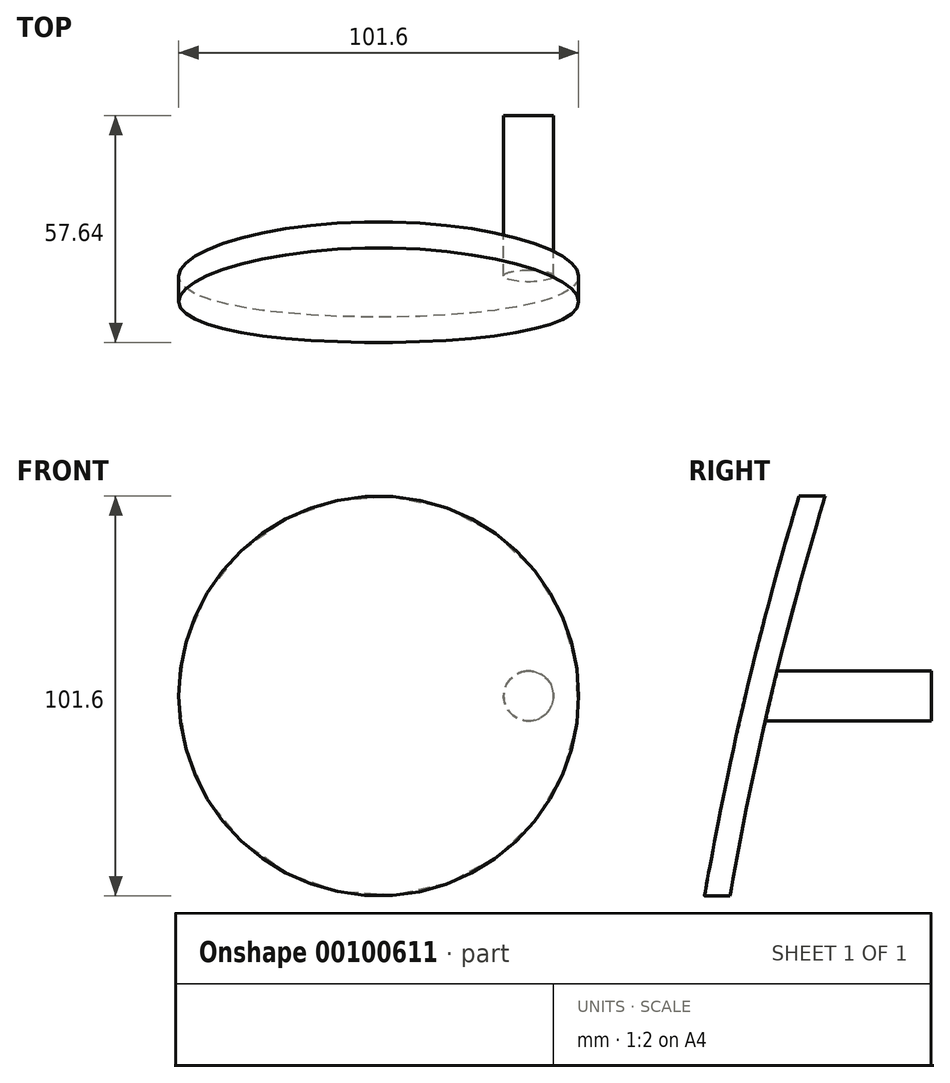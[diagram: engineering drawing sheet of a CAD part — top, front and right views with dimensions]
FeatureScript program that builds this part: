
annotation { "Feature Type Name" : "Feature", "Feature Type Description" : "" }
export const myFeature = defineFeature(function(context is Context, id is Id, definition is map)
    precondition{}
    {
        {
            var Q0;
            Q0=qCreatedBy(makeId("Right.planeOp"),FACE);
            var sketch = newSketch(context, id + "F0", { "sketchPlane" : qUnion([Q0])});
            skArc(sketch, "E0", {"start": v(-794.07, 323.85) * mm, "mid": v(-857.57, 0) * mm, "end": v(-794.07, -323.85) * mm});
            skLineSegment(sketch, "E1", {"start": v(-794.07, 323.85) * mm, "end": v(-794.07, -323.85) * mm});
            skSolve(sketch);
        }
        {
            var Q0;
            Q0 = qSketchRegion(id + "F0", true);
            extrude(context, id + "F1", {"entities" : qUnion([Q0]), "endBound" : BoundingType.SYMMETRIC, "depth" : 101.6 * mm});
        }
        {
            var Q0;
            Q0=qCreatedBy(makeId("Right.planeOp"),FACE);
            var sketch = newSketch(context, id + "F2", { "sketchPlane" : qUnion([Q0])});
            skCircle(sketch, "E2", {"center": v(0, 0) * mm, "radius": 851.22 * mm});
            skSolve(sketch);
        }
        {
            var Q0;
            Q0 = qSketchRegion(id + "F2", true);
            extrude(context, id + "F3", {"entities" : qUnion([Q0]), "operationType" : NewBodyOperationType.REMOVE, "endBound" : BoundingType.SYMMETRIC, "oppositeDirection" : true, "depth" : 101.6 * mm});
        }
        {
            var Q0;
            Q0=qCreatedBy(makeId("Front.planeOp"),FACE);
            var sketch = newSketch(context, id + "F4", { "sketchPlane" : qUnion([Q0])});
            skCircle(sketch, "E3", {"center": v(0, 196.85) * mm, "radius": 50.8 * mm});
            skLineSegment(sketch, "E4.bottom", {"start": v(-127, 381) * mm, "end": v(127, 381) * mm});
            skLineSegment(sketch, "E4.top", {"start": v(-127, -381) * mm, "end": v(127, -381) * mm});
            skLineSegment(sketch, "E4.left", {"start": v(-127, 381) * mm, "end": v(-127, -381) * mm});
            skLineSegment(sketch, "E4.right", {"start": v(127, 381) * mm, "end": v(127, -381) * mm});
            skSolve(sketch);
        }
        {
            var Q0;
            Q0=makeQuery(id+"F4.imprint","IMPRINT",FACE,{"disambiguationData":[TD([[makeQuery(id+"F4.imprint","IMPRINT",EDGE,{"derivedFrom":sQuery(id+"F4.wireOp",EDGE,"E3")}),-1.0]])]});
            extrude(context, id + "F5", {"entities" : qUnion([Q0]), "operationType" : NewBodyOperationType.REMOVE, "endBound" : BoundingType.THROUGH_ALL, "depth" : 25.4 * mm});
        }
        {
            var Q0;
            Q0=qCreatedBy(makeId("Front.planeOp"),FACE);
            cPlane(context, id + "F6", {"entities" : qUnion([Q0]), "cplaneType" : CPlaneType.OFFSET, "offset" : 787.4 * mm, "width" : 152.4 * mm, "height" : 152.4 * mm});
        }
        {
            var Q0;
            Q0=qCreatedBy(id+"F6.planeOp",FACE);
            var sketch = newSketch(context, id + "F7", { "sketchPlane" : qUnion([Q0])});
            skCircle(sketch, "E5", {"center": v(38.1, 196.85) * mm, "radius": 6.35 * mm});
            skSolve(sketch);
        }
        {
            var Q0;
            Q0=makeQuery(id+"F7.imprint","IMPRINT",FACE,{"disambiguationData":[TD([[makeQuery(id+"F7.imprint","IMPRINT",EDGE,{"derivedFrom":sQuery(id+"F7.wireOp",EDGE,"E5")}),1.0]])]});
            extrude(context, id + "F8", {"entities" : qUnion([Q0]), "operationType" : NewBodyOperationType.ADD, "endBound" : BoundingType.UP_TO_NEXT, "depth" : 50.8 * mm});
        }
    });
